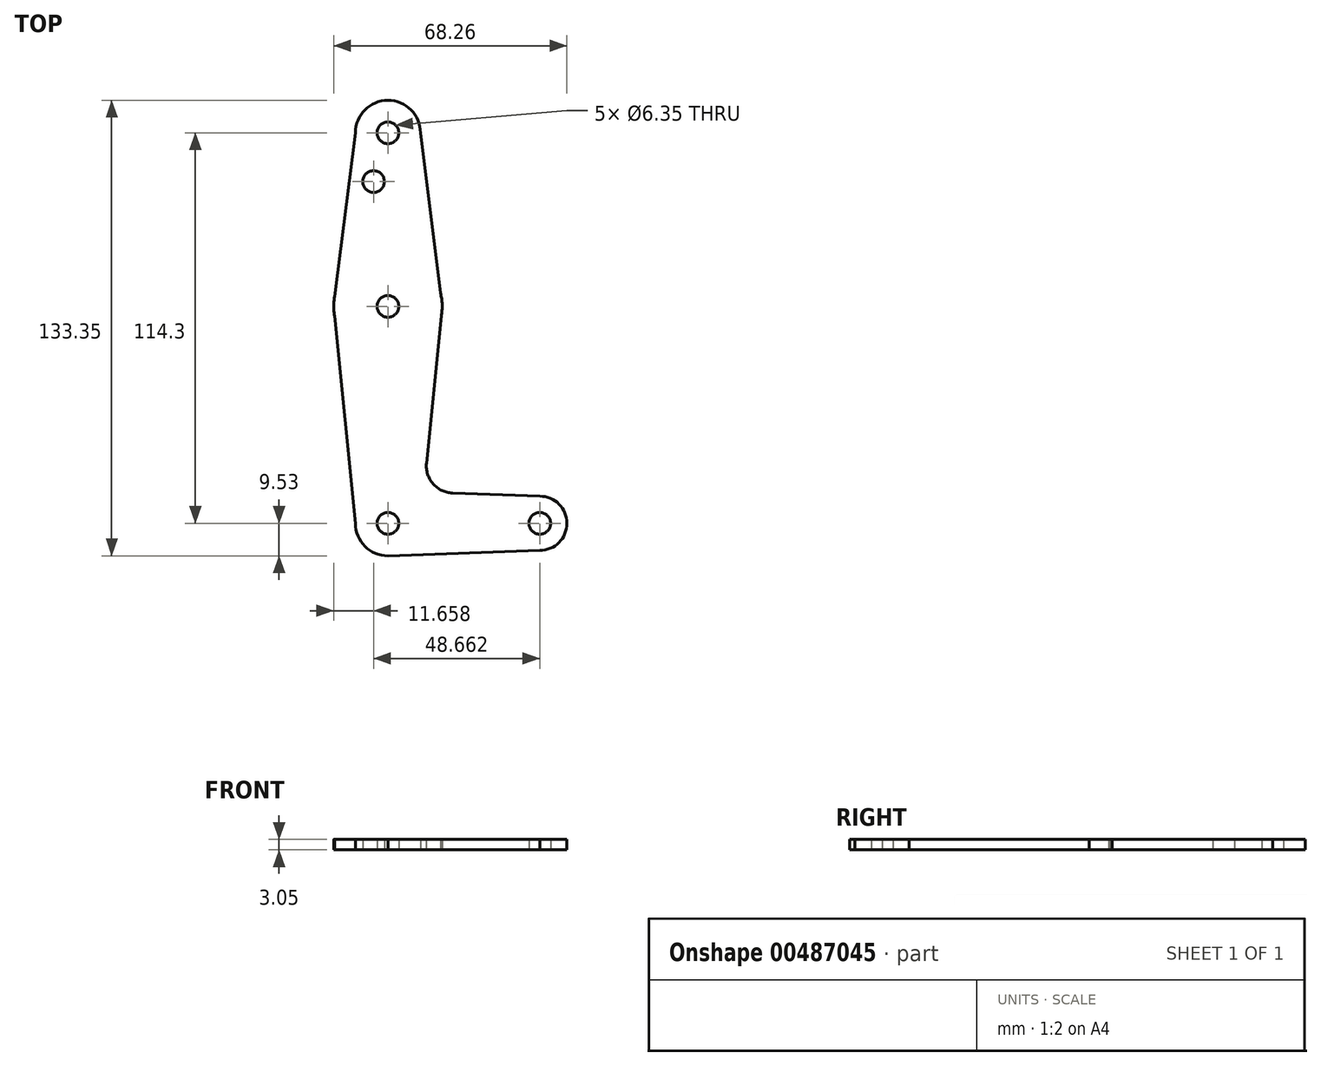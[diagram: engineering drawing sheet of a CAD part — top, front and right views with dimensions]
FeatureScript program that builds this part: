
annotation { "Feature Type Name" : "Feature", "Feature Type Description" : "" }
export const myFeature = defineFeature(function(context is Context, id is Id, definition is map)
    precondition{}
    {
        {
            var Q0;
            Q0=qCreatedBy(makeId("Top.planeOp"),FACE);
            var sketch = newSketch(context, id + "F0", { "sketchPlane" : qUnion([Q0])});
            skCircle(sketch, "E0", {"center": v(0, 0) * mm, "radius": 15.88 * mm});
            skCircle(sketch, "E1", {"center": v(0, 0) * mm, "radius": 3.18 * mm});
            skLineSegment(sketch, "E2", {"start": v(0, 0) * mm, "end": v(0, -63.5) * mm, "construction": true});
            skCircle(sketch, "E3", {"center": v(0, -63.5) * mm, "radius": 9.53 * mm});
            skCircle(sketch, "E4", {"center": v(0, -63.5) * mm, "radius": 3.18 * mm});
            skLineSegment(sketch, "E5", {"start": v(0, -63.5) * mm, "end": v(44.45, -63.5) * mm});
            skCircle(sketch, "E6", {"center": v(44.45, -63.5) * mm, "radius": 7.94 * mm});
            skCircle(sketch, "E7", {"center": v(44.45, -63.5) * mm, "radius": 3.18 * mm});
            skLineSegment(sketch, "E8", {"start": v(18.92, -54.65) * mm, "end": v(44.45, -55.56) * mm});
            skLineSegment(sketch, "E9", {"start": v(-9.52, -63.5) * mm, "end": v(-15.62, -2.85) * mm});
            skLineSegment(sketch, "E10", {"start": v(11.3, -45.91) * mm, "end": v(15.62, -2.85) * mm});
            skArc(sketch, "E11.filletArc", {"start": v(11.3, -45.91) * mm, "mid": v(13.21, -51.93) * mm, "end": v(18.92, -54.65) * mm});
            skLineSegment(sketch, "E12", {"start": v(0, -63.5) * mm, "end": v(0, 50.8) * mm, "construction": true});
            skCircle(sketch, "E13", {"center": v(0, 50.8) * mm, "radius": 3.18 * mm});
            skCircle(sketch, "E14", {"center": v(0, 50.8) * mm, "radius": 9.53 * mm});
            skLineSegment(sketch, "E15", {"start": v(0, 0) * mm, "end": v(0, 36.53) * mm, "construction": true});
            skCircle(sketch, "E16", {"center": v(-4.21, 36.53) * mm, "radius": 3.18 * mm});
            skLineSegment(sketch, "E17", {"start": v(-9.53, 50.8) * mm, "end": v(-15.62, 2.85) * mm});
            skLineSegment(sketch, "E18", {"start": v(9.53, 50.8) * mm, "end": v(15.39, 3.9) * mm});
            skLineSegment(sketch, "E19", {"start": v(0, -73.02) * mm, "end": v(44.45, -71.44) * mm});
            skSolve(sketch);
        }
        {
            var Q0;
            Q0=makeQuery(id+"F0.imprint","IMPRINT",FACE,{"disambiguationData":[TD([[makeQuery(id+"F0.imprint","IMPRINT",EDGE,{"derivedFrom":sQuery(id+"F0.wireOp",EDGE,"E13")}),-1.0]])]});
            var Q1;
            Q1=makeQuery(id+"F0.imprint","IMPRINT",FACE,{"disambiguationData":[TD([[makeQuery(id+"F0.imprint","IMPRINT",EDGE,{"derivedFrom":sQuery(id+"F0.wireOp",EDGE,"E16")}),-1.0]])]});
            var Q2;
            Q2=makeQuery(id+"F0.imprint","IMPRINT",FACE,{"disambiguationData":[TD([[makeQuery(id+"F0.imprint","IMPRINT",EDGE,{"derivedFrom":sQuery(id+"F0.wireOp",EDGE,"E1")}),-1.0]])]});
            var Q3;
            {var subQ0=sQuery(id+"F0.wireOp",EDGE,"E8");Q3=makeQuery(id+"F0.imprint","IMPRINT",FACE,{"disambiguationData":[TD([[makeQuery(id+"F0.imprint","IMPRINT",EDGE,{"derivedFrom":subQ0}),-1.0]])]});}
            var Q4;
            Q4=makeQuery(id+"F0.imprint","IMPRINT",FACE,{"disambiguationData":[TD([[makeQuery(id+"F0.imprint","IMPRINT",EDGE,{"derivedFrom":sQuery(id+"F0.wireOp",EDGE,"E4")}),-1.0]])]});
            var Q5;
            {var subQ0=sQuery(id+"F0.wireOp",EDGE,"E5");var subQ1=sQuery(id+"F0.wireOp",EDGE,"E3");var subQ2=makeQuery(id+"F0.imprint","INTERSECT",VERTEX,{"derivedFrom":[subQ1,subQ0]});Q5=makeQuery(id+"F0.imprint","IMPRINT",FACE,{"disambiguationData":[TD([[makeQuery(id+"F0.imprint","IMPRINT",EDGE,{"disambiguationData":[TD([[subQ2,1.0]])],"derivedFrom":subQ1}),-1.0]])]});}
            var Q6;
            Q6=makeQuery(id+"F0.imprint","IMPRINT",FACE,{"disambiguationData":[TD([[makeQuery(id+"F0.imprint","IMPRINT",EDGE,{"derivedFrom":sQuery(id+"F0.wireOp",EDGE,"E7")}),-1.0]])]});
            extrude(context, id + "F1", {"entities" : qUnion([Q0, Q1, Q2, Q3, Q4, Q5, Q6]), "depth" : 3.05 * mm});
        }
    });
